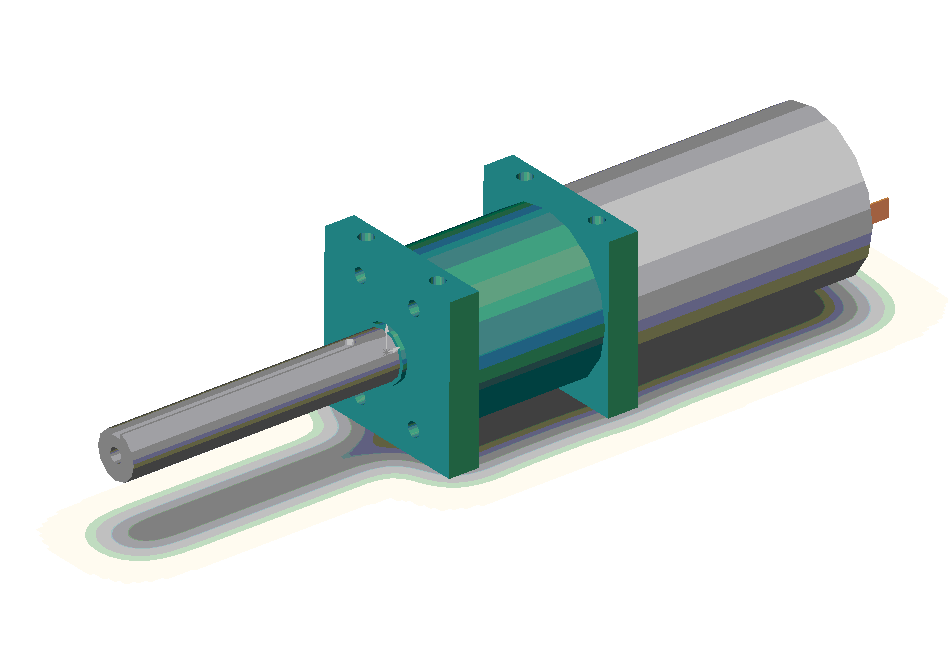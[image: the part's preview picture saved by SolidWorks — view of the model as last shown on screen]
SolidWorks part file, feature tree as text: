
SOLIDWORKS PART (.sldprt)
format: sldprt  version: not decoded by parser v0  size: 543,744 bytes
history: native  units: mm
features: sketch x13, extrude x8, cut_extrude x5, plane x1 (+8 scaffold rows collapsed)
feature tree (35):
  scaffold x8  (default folders/planes/origin — collapsed)
  sketch  "Sketch1"  dims[D1=44.4mm D2=44.4mm D3=22.2mm D4=22.2mm]
  extrude  "Base-Extrude"  Depth=8.3mm
  sketch  "Sketch2"  dims[D1=42.0mm]
  extrude  "Boss-Extrude1"  Depth=53mm
  sketch  "Sketch3"
  extrude  "Boss-Extrude2"  Depth=8.3mm
  sketch  "Sketch4"  dims[D1=42.0mm]
  extrude  "Boss-Extrude3"  Depth=67mm
  sketch  "Sketch5"  dims[D1=12.7mm]
  extrude  "Boss-Extrude4"  Depth=76.2mm
  plane  "Plane1"  Offset=4.7625mm
  sketch  "Sketch6"  dims[D2=3.175mm D1=10.8mm D3=3.175mm]
  cut_extrude  "Cut-Extrude1"  [1 undecoded]
  sketch  "Sketch7"  dims[D1=4.0386mm]
  cut_extrude  "Cut-Extrude2"  Depth=12.7mm
  sketch  "Sketch8"  dims[c1.D4=4.04mm c1.D5=4.04mm c1.D9=4.04mm c1.D10=4.04mm c1.D1=12.7mm c1.D2=25.4mm c1.D3=4.15mm c2.D4=44.4mm c2.D6=4.15mm c2.D7=44.7mm c2.D8=44.7mm c2.D11=12.7mm c2.D12=25.4mm]
  cut_extrude  "Cut-Extrude3"  Depth=9.525mm
  sketch  "Sketch9"  dims[c1.D1=4.04mm c1.D2=4.04mm c1.D3=4.04mm c1.D4=4.04mm c2.D1=4.15mm]
  cut_extrude  "Cut-Extrude4"  Depth=9.525mm
  sketch  "Sketch11"  dims[D1=~14.649265mm]
  extrude  "Boss-Extrude5"  Depth=1.25mm
  sketch  "Sketch12"  dims[D1=21.0mm]
  extrude  "Boss-Extrude6"  Depth=4mm
  sketch  "Sketch13"  dims[D1=16.0mm D2=16.0mm D3=2.5mm D4=2.5mm D5=0.5mm D6=0.5mm D7=5.0mm D8=5.0mm]
  extrude  "Boss-Extrude7"  Depth=8mm
  sketch  "Sketch14"  dims[D7=4.04mm D8=4.04mm D9=4.04mm D10=4.04mm D1=9.525mm D2=9.525mm D3=9.5253mm D4=9.525mm D5=15.25mm D6=30.48mm]
  cut_extrude  "Cut-Extrude5"  Depth=9.525mm
decode coverage: 24 of 26 modeling features carry decoded parameters
note: ~ marks probable driven/reference dimensions
note: 1 parameter value undecoded
note: suppression state not decoded; provenance and decode notes live in map.json
